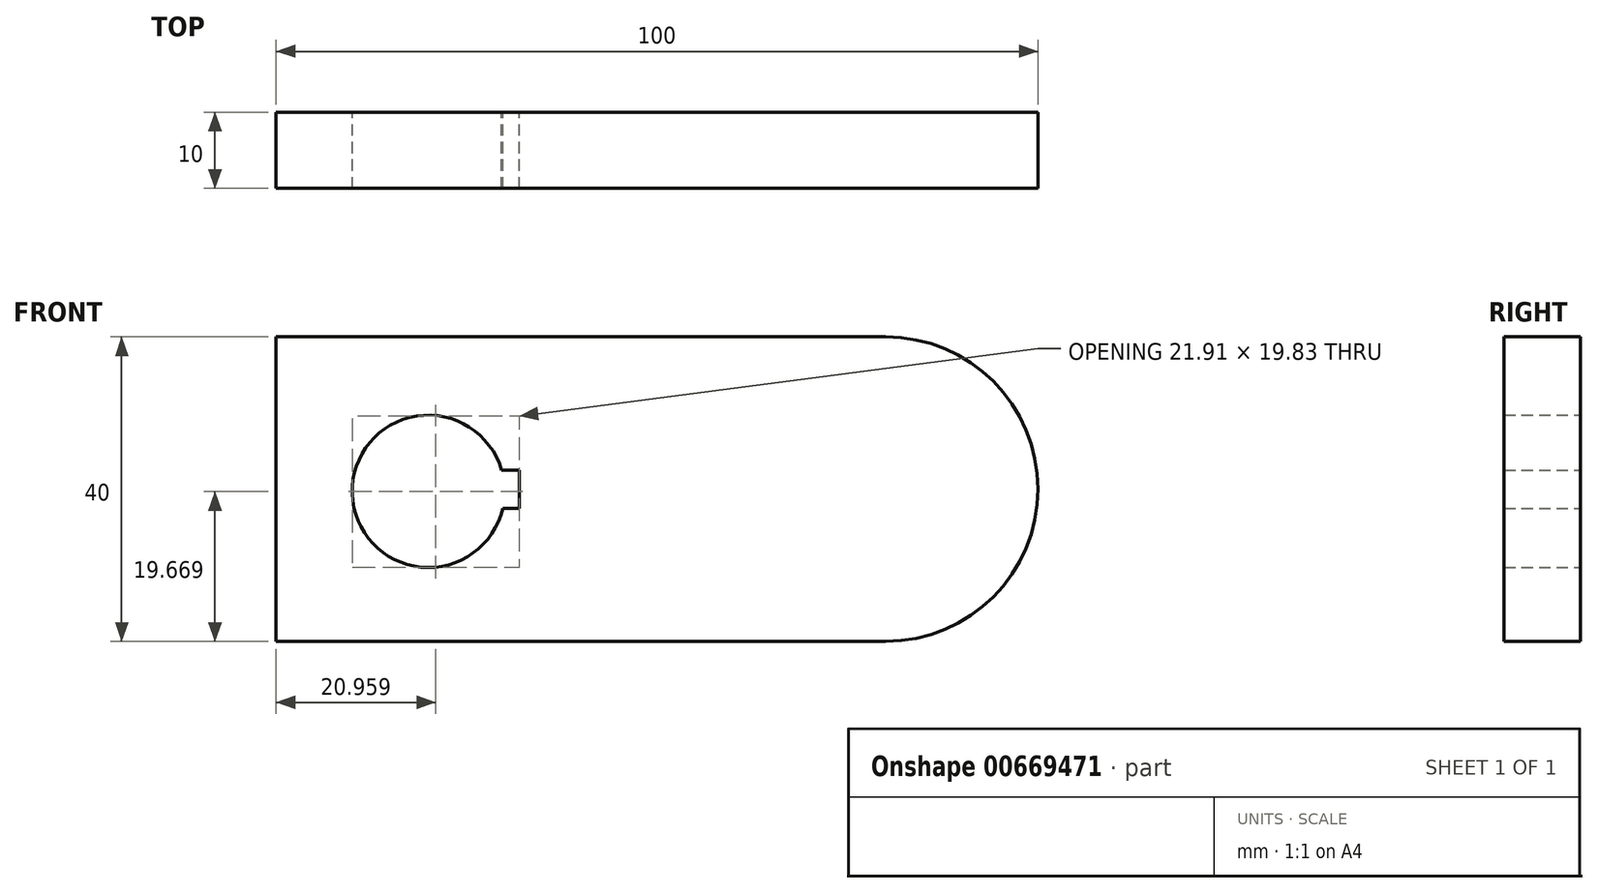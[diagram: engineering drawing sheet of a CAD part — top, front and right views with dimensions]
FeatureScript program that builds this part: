
annotation { "Feature Type Name" : "Feature", "Feature Type Description" : "" }
export const myFeature = defineFeature(function(context is Context, id is Id, definition is map)
    precondition{}
    {
        {
            var Q0;
            Q0=qCreatedBy(makeId("Front.planeOp"),FACE);
            var sketch = newSketch(context, id + "F0", { "sketchPlane" : qUnion([Q0])});
            skLineSegment(sketch, "E0", {"start": v(-20, 0) * mm, "end": v(-100, 0) * mm});
            skLineSegment(sketch, "E1", {"start": v(-100, 0) * mm, "end": v(-100, 40) * mm});
            skLineSegment(sketch, "E2", {"start": v(-100, 40) * mm, "end": v(-20, 40) * mm});
            skArc(sketch, "E3", {"start": v(-70.4, 22.5) * mm, "mid": v(-90, 19.4) * mm, "end": v(-70.25, 17.5) * mm});
            skPoint(sketch, "E4.startSnap0", {"position": v(-100, 20) * mm});
            skPoint(sketch, "E4.endSnap0", {"position": v(-100, 20) * mm});
            skArc(sketch, "E5", {"start": v(-20, 0) * mm, "mid": v(0, 20) * mm, "end": v(-20, 40) * mm});
            skPoint(sketch, "E6.start.orphan", {"position": v(0, 40) * mm});
            skPoint(sketch, "E4.start.orphan", {"position": v(-100, 19.7) * mm});
            skLineSegment(sketch, "E7.bottom", {"start": v(-70.4, 22.5) * mm, "end": v(-68.09, 22.5) * mm});
            skLineSegment(sketch, "E7.top", {"start": v(-70.25, 17.5) * mm, "end": v(-68.09, 17.5) * mm});
            skLineSegment(sketch, "E7.right", {"start": v(-68.09, 22.5) * mm, "end": v(-68.09, 17.5) * mm});
            skSolve(sketch);
        }
        {
            var Q0;
            Q0=makeQuery(id+"F0.imprint","IMPRINT",FACE,{"disambiguationData":[TD([[makeQuery(id+"F0.imprint","IMPRINT",EDGE,{"derivedFrom":sQuery(id+"F0.wireOp",EDGE,"E0")}),-1.0]])]});
            extrude(context, id + "F1", {"entities" : qUnion([Q0]), "depth" : 10 * mm, "offsetDistance" : 25 * mm});
        }
    });
